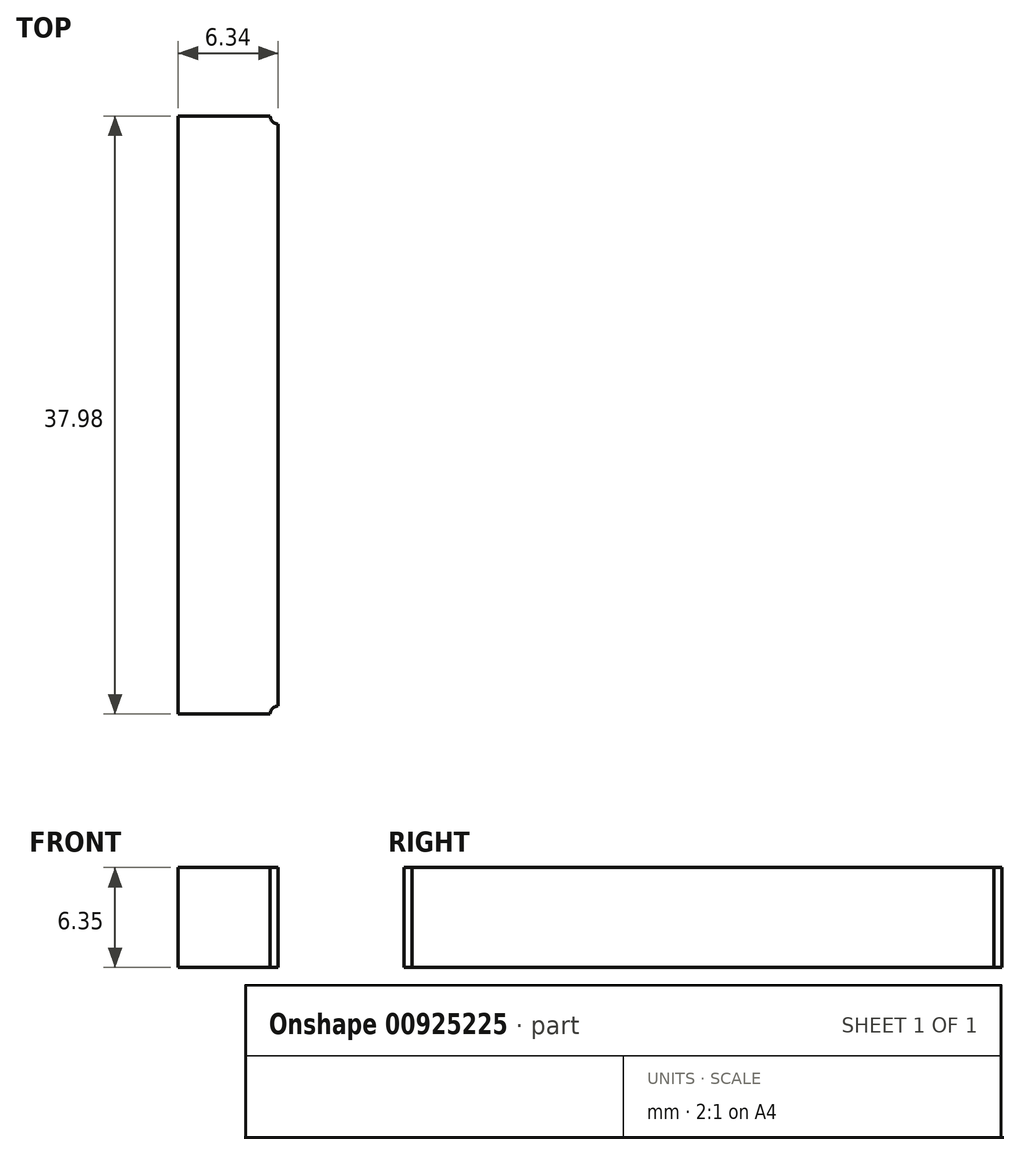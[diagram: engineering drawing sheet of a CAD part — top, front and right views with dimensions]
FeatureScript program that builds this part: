
annotation { "Feature Type Name" : "Feature", "Feature Type Description" : "" }
export const myFeature = defineFeature(function(context is Context, id is Id, definition is map)
    precondition{}
    {
        {
            var Q0;
            Q0=qCreatedBy(makeId("Top.planeOp"),FACE);
            var sketch = newSketch(context, id + "F0", { "sketchPlane" : qUnion([Q0])});
            skLineSegment(sketch, "E0.bottom", {"start": v(66.68, -50.8) * mm, "end": v(-66.68, -50.8) * mm});
            skLineSegment(sketch, "E0.top", {"start": v(66.68, 50.8) * mm, "end": v(-66.68, 50.8) * mm});
            skLineSegment(sketch, "E0.left", {"start": v(66.68, -50.8) * mm, "end": v(66.67, 50.8) * mm});
            skLineSegment(sketch, "E0.right", {"start": v(-66.67, -50.8) * mm, "end": v(-66.68, 50.8) * mm});
            skPoint(sketch, "E0.middle", {"position": v(0, 0) * mm});
            skSolve(sketch);
        }
        {
            var Q0;
            Q0=qSketchRegion(id+"F0",true);
            extrude(context, id + "F1", {"entities" : qUnion([Q0]), "depth" : 6.35 * mm, "offsetDistance" : 25.4 * mm});
        }
        {
            var Q0;
            Q0=makeQuery(id+"F1.opExtrude","CAP_FACE",FACE,{"disambiguationData":[OSD([sQuery(id+"F0.wireOp",EDGE,"E0.bottom"),sQuery(id+"F0.wireOp",EDGE,"E0.top"),sQuery(id+"F0.wireOp",EDGE,"E0.left"),sQuery(id+"F0.wireOp",EDGE,"E0.right")])],"isStart":false});
            var sketch = newSketch(context, id + "F2", { "sketchPlane" : qUnion([Q0])});
            skLineSegment(sketch, "E1.bottom", {"start": v(-73.03, 18.99) * mm, "end": v(-66.68, 18.99) * mm});
            skLineSegment(sketch, "E1.top", {"start": v(-73.03, -18.99) * mm, "end": v(-66.68, -18.99) * mm});
            skLineSegment(sketch, "E1.left", {"start": v(-66.68, 18.99) * mm, "end": v(-66.68, -18.99) * mm});
            skLineSegment(sketch, "E1.right", {"start": v(-73.02, 18.99) * mm, "end": v(-73.02, -18.99) * mm});
            skLineSegment(sketch, "E2.bottom", {"start": v(73.02, 18.99) * mm, "end": v(66.68, 18.99) * mm});
            skLineSegment(sketch, "E2.top", {"start": v(73.02, -18.99) * mm, "end": v(66.68, -18.99) * mm});
            skLineSegment(sketch, "E2.left", {"start": v(66.68, 18.99) * mm, "end": v(66.68, -18.99) * mm});
            skLineSegment(sketch, "E2.right", {"start": v(73.03, 18.99) * mm, "end": v(73.03, -18.99) * mm});
            skLineSegment(sketch, "E3", {"start": v(-66.68, 0) * mm, "end": v(66.68, 0) * mm, "construction": true});
            skSolve(sketch);
        }
        {
            var Q0;
            Q0=qSketchRegion(id+"F2",true);
            extrude(context, id + "F3", {"entities" : qUnion([Q0]), "operationType" : NewBodyOperationType.ADD, "oppositeDirection" : true, "depth" : 6.35 * mm, "offsetDistance" : 25.4 * mm});
        }
        {
            var Q0;
            Q0=makeQuery(id+"F1.opExtrude","CAP_FACE",FACE,{"disambiguationData":[OSD([sQuery(id+"F0.wireOp",EDGE,"E0.bottom"),sQuery(id+"F0.wireOp",EDGE,"E0.top"),sQuery(id+"F0.wireOp",EDGE,"E0.left"),sQuery(id+"F0.wireOp",EDGE,"E0.right")])],"isStart":false});
            var sketch = newSketch(context, id + "F4", { "sketchPlane" : qUnion([Q0])});
            skLineSegment(sketch, "E4.bottom", {"start": v(-63.5, 41.28) * mm, "end": v(63.5, 41.28) * mm});
            skLineSegment(sketch, "E4.top", {"start": v(-63.5, 7.94) * mm, "end": v(63.5, 7.94) * mm});
            skLineSegment(sketch, "E4.left", {"start": v(-63.5, 41.28) * mm, "end": v(-63.5, 7.94) * mm});
            skLineSegment(sketch, "E4.right", {"start": v(63.5, 41.28) * mm, "end": v(63.5, 7.94) * mm});
            skLineSegment(sketch, "E5.bottom", {"start": v(-63.5, 4.76) * mm, "end": v(63.5, 4.76) * mm});
            skLineSegment(sketch, "E5.top", {"start": v(-63.5, -46.04) * mm, "end": v(63.5, -46.04) * mm});
            skLineSegment(sketch, "E5.left", {"start": v(-63.5, 4.76) * mm, "end": v(-63.5, -46.04) * mm});
            skLineSegment(sketch, "E5.right", {"start": v(63.5, 4.76) * mm, "end": v(63.5, -46.04) * mm});
            skPoint(sketch, "E6", {"position": v(0, 41.28) * mm});
            skSolve(sketch);
        }
        {
            var Q0;
            Q0=qSketchRegion(id+"F4",true);
            extrude(context, id + "F5", {"entities" : qUnion([Q0]), "operationType" : NewBodyOperationType.ADD, "depth" : 3.17 * mm, "offsetDistance" : 25.4 * mm});
        }
        {
            var Q0;
            Q0=makeQuery(id+"F5.opExtrude","CAP_FACE",FACE,{"disambiguationData":[OSD([sQuery(id+"F4.wireOp",EDGE,"E5.bottom"),sQuery(id+"F4.wireOp",EDGE,"E5.top"),sQuery(id+"F4.wireOp",EDGE,"E5.left"),sQuery(id+"F4.wireOp",EDGE,"E5.right")])],"isStart":false});
            var sketch = newSketch(context, id + "F6", { "sketchPlane" : qUnion([Q0])});
            skLineSegment(sketch, "E7.bottom", {"start": v(-12.7, -46.04) * mm, "end": v(-9.52, -46.04) * mm});
            skLineSegment(sketch, "E7.top", {"start": v(-12.7, 4.76) * mm, "end": v(-9.52, 4.76) * mm});
            skLineSegment(sketch, "E7.left", {"start": v(-12.7, -46.04) * mm, "end": v(-12.7, 4.76) * mm});
            skLineSegment(sketch, "E7.right", {"start": v(-9.52, -46.04) * mm, "end": v(-9.52, 4.76) * mm});
            skSolve(sketch);
        }
        {
            var Q0;
            Q0 = qSketchRegion(id + "F6", true);
            extrude(context, id + "F7", {"entities" : qUnion([Q0]), "operationType" : NewBodyOperationType.REMOVE, "oppositeDirection" : true, "depth" : 3.17 * mm, "offsetDistance" : 25.4 * mm});
        }
        {
            var Q0;
            Q0=makeQuery(id+"F3.boolean.opBoolean","MERGE",FACE,{"derivedFrom":[makeQuery(id+"F1.opExtrude","CAP_FACE",FACE,{"disambiguationData":[OSD([sQuery(id+"F0.wireOp",EDGE,"E0.bottom"),sQuery(id+"F0.wireOp",EDGE,"E0.top"),sQuery(id+"F0.wireOp",EDGE,"E0.left"),sQuery(id+"F0.wireOp",EDGE,"E0.right")])],"isStart":true}),makeQuery(id+"F3.opExtrude","CAP_FACE",FACE,{"disambiguationData":[OSD([sQuery(id+"F2.wireOp",EDGE,"E1.bottom"),sQuery(id+"F2.wireOp",EDGE,"E1.top"),sQuery(id+"F2.wireOp",EDGE,"E1.left"),sQuery(id+"F2.wireOp",EDGE,"E1.right")])],"isStart":false}),makeQuery(id+"F3.opExtrude","CAP_FACE",FACE,{"disambiguationData":[OSD([sQuery(id+"F2.wireOp",EDGE,"E2.bottom"),sQuery(id+"F2.wireOp",EDGE,"E2.top"),sQuery(id+"F2.wireOp",EDGE,"E2.left"),sQuery(id+"F2.wireOp",EDGE,"E2.right")])],"isStart":false})]});
            var sketch = newSketch(context, id + "F8", { "sketchPlane" : qUnion([Q0])});
            skArc(sketch, "E8", {"start": v(-66.68, 19.5) * mm, "mid": v(-66.32, 18.63) * mm, "end": v(-67.18, 18.99) * mm});
            skArc(sketch, "E9", {"start": v(-66.68, -19.5) * mm, "mid": v(-66.32, -18.63) * mm, "end": v(-67.18, -18.99) * mm});
            skArc(sketch, "E10", {"start": v(66.68, -19.5) * mm, "mid": v(66.32, -18.63) * mm, "end": v(67.18, -18.99) * mm});
            skArc(sketch, "E11", {"start": v(67.18, 18.99) * mm, "mid": v(66.32, 18.63) * mm, "end": v(66.67, 19.5) * mm});
            skLineSegment(sketch, "E12", {"start": v(66.68, 18.99) * mm, "end": v(66.68, 19.5) * mm});
            skLineSegment(sketch, "E13", {"start": v(66.68, 18.99) * mm, "end": v(67.18, 18.99) * mm});
            skLineSegment(sketch, "E14", {"start": v(66.68, -18.99) * mm, "end": v(66.68, -19.5) * mm});
            skLineSegment(sketch, "E15", {"start": v(66.68, -18.99) * mm, "end": v(67.18, -18.99) * mm});
            skLineSegment(sketch, "E16", {"start": v(-66.68, -18.99) * mm, "end": v(-67.18, -18.99) * mm});
            skLineSegment(sketch, "E17", {"start": v(-66.68, -18.99) * mm, "end": v(-66.68, -19.5) * mm});
            skLineSegment(sketch, "E18", {"start": v(-66.68, 18.99) * mm, "end": v(-67.18, 18.99) * mm});
            skLineSegment(sketch, "E19", {"start": v(-66.68, 18.99) * mm, "end": v(-66.68, 19.5) * mm});
            skSolve(sketch);
        }
        {
            var Q0;
            Q0 = qSketchRegion(id + "F8", true);
            var Q1;
            Q1=makeQuery(id+"F8.imprint","IMPRINT",FACE,{"disambiguationData":[TD([[makeQuery(id+"F8.imprint","IMPRINT",EDGE,{"derivedFrom":sQuery(id+"F8.wireOp",EDGE,"E8")}),-1.0]])]});
            var Q2;
            Q2=makeQuery(id+"F8.imprint","IMPRINT",FACE,{"disambiguationData":[TD([[makeQuery(id+"F8.imprint","IMPRINT",EDGE,{"derivedFrom":sQuery(id+"F8.wireOp",EDGE,"E11")}),-1.0]])]});
            var Q3;
            Q3=makeQuery(id+"F8.imprint","IMPRINT",FACE,{"disambiguationData":[TD([[makeQuery(id+"F8.imprint","IMPRINT",EDGE,{"derivedFrom":sQuery(id+"F8.wireOp",EDGE,"E10")}),-1.0]])]});
            var Q4;
            Q4=makeQuery(id+"F8.imprint","IMPRINT",FACE,{"disambiguationData":[TD([[makeQuery(id+"F8.imprint","IMPRINT",EDGE,{"derivedFrom":sQuery(id+"F8.wireOp",EDGE,"E9")}),1.0]])]});
            extrude(context, id + "F9", {"entities" : qUnion([Q0, Q1, Q2, Q3, Q4]), "operationType" : NewBodyOperationType.REMOVE, "endBound" : BoundingType.THROUGH_ALL, "oppositeDirection" : true, "depth" : 25.4 * mm, "offsetDistance" : 25.4 * mm});
        }
    });
